# Revit family: Lighting_Controller-Lutron-Energi_Savr_Node-QSNE-2DAL-D---
name_source: partatom
category: Lighting Devices
revit_build: Autodesk Revit 2015 (Build: 20160512_0715(x64)
units: mm (PartAtom-declared; Revit-internal decimal feet)

## types (1)
- ERROR_LOAD TYPE CATALOG
    Assembly Code = D3060800
    Center Face Height = 45 mm  [stored 0.147638 ft]
    Controller Enclosure Material = Plastic - Lutron - Gray
    DIN Rail Depth = 8 mm  [stored 0.0262467 ft]
    DIN Rail Height = 35 mm
    Default Elevation = 1219 mm
    Description = Energi Savr Node with DALI (CE) - DIN-rail
    ENGworks URL = http://www.ENGworks.com
    Fin Width = 3 mm  [stored 0.00984252 ft]
    Input Voltage = 240 V
    Label = LC
    Load Classification = Lighting
    Manufacturer = Lutron Electronics
    Maximum DALI Compliant Load Quantity = 64
    Maximum Device Quantity Per Bus = 100
    Maximum Operating Temperature = 40 °C
    Maximum Supply Amperage Per Bus = 250 mA
    Maximum Zone Quantity = 16
    Model = QSNE-2DAL-D
    Module Void Width = 50 mm  [stored 0.164042 ft]
    Output Voltage = 18 V
    Overall Depth = 61 mm
    Overall Height = 90 mm
    Overall Width = 162 mm
    Product Page URL = http://www.lutron.com
    Series = DALI
    Thomas Enterprise Solutions URL = http://www.thomasenterprisesolutions.com
    Tier 1 Bend = 18 mm  [stored 0.0590551 ft]
    URL = http://www.lutron.com
    Version = 1

note: [stored X ft] marks values corroborated as IEEE doubles in the binary element streams (Revit-internal decimal feet)

## geometry (parser evidence)
native form markers: Sweep x4
no freeform markers — native parametric forms only
